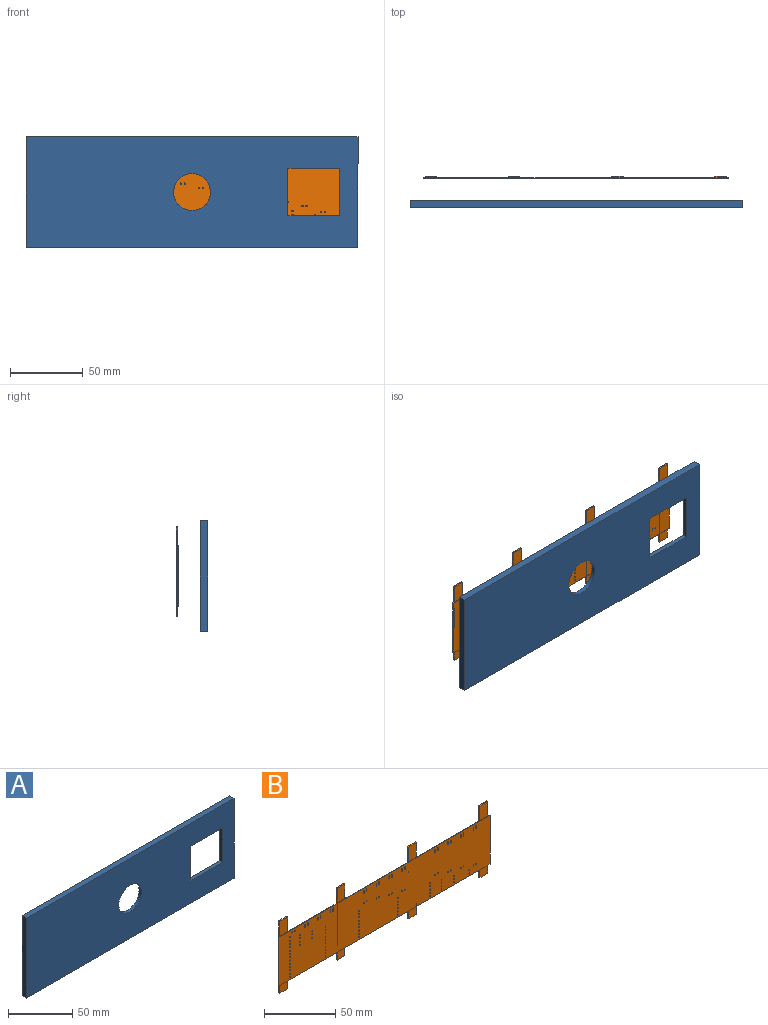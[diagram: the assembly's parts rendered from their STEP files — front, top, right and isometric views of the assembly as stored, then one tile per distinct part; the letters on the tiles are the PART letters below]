
ASSEMBLY  parts=2 mates=1
PART A: 48 faces, bbox 228.6x5.1x76.2 mm
  f0: plane 228.6x76.2mm, normal (0,-1,0), area 15738.4mm2, adj f11,f12,f13,f14,f43,f44,f45,f46
  f1: plane 210.9x62.26mm, normal (0,1,0), area 7928.5mm2, adj f3,f4,f5,f6,f7,f8,f9,f10
  f2: plane 228.6x76.2mm, normal (0,1,0), area 7810mm2, adj f3,f4,f5,f6,f7,f8,f9,f10
  f3: plane 48.84x2.03mm, normal (0,0,1), area 99.3mm2, adj f1,f2,f37,f42
  f4: plane 62.81x2.03mm, normal (0,0,1), area 127.6mm2, adj f1,f2,f33,f39
  f5: plane 2.03x1.61mm, normal (0,0,1), area 3.3mm2, adj f1,f2,f18,f36
  f6: plane 62.81x2.03mm, normal (0,0,1), area 127.6mm2, adj f1,f2,f31,f34
  f7: plane 48.84x2.03mm, normal (0,0,-1), area 99.3mm2, adj f1,f2,f25,f29
  f8: plane 62.81x2.03mm, normal (0,0,-1), area 127.6mm2, adj f1,f2,f19,f26
  f9: plane 2.03x1.61mm, normal (0,0,-1), area 3.3mm2, adj f1,f2,f18,f23
  f10: plane 62.81x2.03mm, normal (0,0,-1), area 127.6mm2, adj f1,f2,f20,f22
  f11: plane 228.6x5.08mm, normal (0,0,-1), area 1161.3mm2, adj f0,f2,f12,f14
  f12: plane 76.2x5.08mm, normal (1,0,0), area 387.1mm2, adj f0,f2,f11,f13
  f13: plane 228.6x5.08mm, normal (0,0,1), area 1161.3mm2, adj f0,f2,f12,f14
  f14: plane 76.2x5.08mm, normal (-1,0,0), area 387.1mm2, adj f0,f2,f11,f13
  f15: plane 2.03x1.59mm, normal (0,0,1), area 3.2mm2, adj f1,f2,f16,f40
  f16: plane 42.44x2.03mm, normal (1,0,0), area 86.2mm2, adj f1,f2,f15,f17
  f17: plane 2.03x1.59mm, normal (0,0,-1), area 3.2mm2, adj f1,f2,f16,f28
  f18: plane 42.44x2.03mm, normal (-1,0,0), area 86.2mm2, adj f1,f2,f5,f9
  f19: plane 12.51x2.03mm, normal (1,0,0), area 25.4mm2, adj f1,f2,f8,f21
  f20: plane 12.51x2.03mm, normal (-1,0,0), area 25.4mm2, adj f1,f2,f10,f21
  f21: plane 8.31x2.03mm, normal (0,0,-1), area 16.9mm2, adj f1,f2,f19,f20
  f22: plane 12.51x2.03mm, normal (1,0,0), area 25.4mm2, adj f1,f2,f10,f24
  f23: plane 12.51x2.03mm, normal (-1,0,0), area 25.4mm2, adj f1,f2,f9,f24
  f24: plane 8.31x2.03mm, normal (0,0,-1), area 16.9mm2, adj f1,f2,f22,f23
  f25: plane 12.51x2.03mm, normal (1,0,0), area 25.4mm2, adj f1,f2,f7,f27
  f26: plane 12.51x2.03mm, normal (-1,0,0), area 25.4mm2, adj f1,f2,f8,f27
  f27: plane 8.31x2.03mm, normal (0,0,-1), area 16.9mm2, adj f1,f2,f25,f26
  f28: plane 12.51x2.03mm, normal (1,0,0), area 25.4mm2, adj f1,f2,f17,f30
  f29: plane 12.51x2.03mm, normal (-1,0,0), area 25.4mm2, adj f1,f2,f7,f30
  f30: plane 8.31x2.03mm, normal (0,0,-1), area 16.9mm2, adj f1,f2,f28,f29
  f31: plane 7.3x2.03mm, normal (-1,0,0), area 14.8mm2, adj f1,f2,f6,f32
  f32: plane 8.31x2.03mm, normal (0,0,1), area 16.9mm2, adj f1,f2,f31,f33
  f33: plane 7.3x2.03mm, normal (1,0,0), area 14.8mm2, adj f1,f2,f4,f32
  f34: plane 7.3x2.03mm, normal (1,0,0), area 14.8mm2, adj f1,f2,f6,f35
  f35: plane 8.31x2.03mm, normal (0,0,1), area 16.9mm2, adj f1,f2,f34,f36
  f36: plane 7.3x2.03mm, normal (-1,0,0), area 14.8mm2, adj f1,f2,f5,f35
  f37: plane 7.3x2.03mm, normal (1,0,0), area 14.8mm2, adj f1,f2,f3,f38
  f38: plane 8.31x2.03mm, normal (0,0,1), area 16.9mm2, adj f1,f2,f37,f39
  f39: plane 7.3x2.03mm, normal (-1,0,0), area 14.8mm2, adj f1,f2,f4,f38
  f40: plane 7.3x2.03mm, normal (1,0,0), area 14.8mm2, adj f1,f2,f15,f41
  f41: plane 8.31x2.03mm, normal (0,0,1), area 16.9mm2, adj f1,f2,f40,f42
  f42: plane 7.3x2.03mm, normal (-1,0,0), area 14.8mm2, adj f1,f2,f3,f41
  f43: cylinder r=12.7mm len=25.4mm, axis (0,-1,0), area 243.2mm2, adj f0,f1
  f44: plane 35.56x3.05mm, normal (0,0,1), area 108.4mm2, adj f0,f1,f45,f47
  f45: plane 33.02x3.05mm, normal (1,0,0), area 100.6mm2, adj f0,f1,f44,f46
  f46: plane 35.56x3.05mm, normal (0,0,-1), area 108.4mm2, adj f0,f1,f45,f47
  f47: plane 33.02x3.05mm, normal (-1,0,0), area 100.6mm2, adj f0,f1,f44,f46
PART B: 159 faces, bbox 210.5x1.5x61.9 mm
  f0: plane 42.06x1.6mm, normal (0,1,0), area 67.3mm2, adj f4,f6,f7,f33
  f1: plane 49.23x42.06mm, normal (0,1,0), area 2044.8mm2, adj f4,f6,f26,f35,f38,f53,f54,f63
  f2: plane 63.2x42.06mm, normal (0,1,0), area 2635.9mm2, adj f4,f6,f12,f19,f39,f40,f41,f42
  f3: plane 63.2x42.06mm, normal (0,1,0), area 2635.3mm2, adj f4,f6,f14,f28,f45,f46,f47,f48
  f4: plane 210.52x0.51mm, normal (0,0,-1), area 106.9mm2, adj f0,f1,f2,f3,f5,f7,f8,f9
  f5: plane 42.06x0.51mm, normal (1,0,0), area 21.4mm2, adj f4,f6,f8,f9
  f6: plane 210.52x0.51mm, normal (0,0,1), area 106.9mm2, adj f0,f1,f2,f3,f5,f7,f8,f9
  f7: plane 42.06x0.51mm, normal (-1,0,0), area 21.4mm2, adj f0,f4,f6,f8
  f8: plane 210.52x42.06mm, normal (0,-1,0), area 8783.9mm2, adj f4,f5,f6,f7,f38,f39,f40,f41
  f9: plane 42.06x1.6mm, normal (0,1,0), area 67.3mm2, adj f4,f5,f6,f21
  f10: plane 7.93x7.11mm, normal (0,-1,0), area 56.4mm2, adj f4,f12,f13,f14
  f11: plane 7.93x1.02mm, normal (0,0,1), area 8.1mm2, adj f12,f14,f15,f16
  f12: plane 61.87x1.02mm, normal (1,0,0), area 62.9mm2, adj f2,f10,f11,f13,f15,f16
  f13: plane 7.93x1.02mm, normal (0,0,-1), area 8.1mm2, adj f10,f12,f14,f15
  f14: plane 61.87x1.02mm, normal (-1,0,0), area 62.9mm2, adj f3,f10,f11,f13,f15,f16
  f15: plane 61.87x7.93mm, normal (0,1,0), area 490.3mm2, adj f11,f12,f13,f14
  f16: plane 12.7x7.93mm, normal (0,-1,0), area 100.6mm2, adj f6,f11,f12,f14
  f17: plane 7.93x7.11mm, normal (0,-1,0), area 56.4mm2, adj f4,f18,f19,f21
  f18: plane 7.93x1.02mm, normal (0,0,-1), area 8.1mm2, adj f17,f19,f21,f22
  f19: plane 61.87x1.02mm, normal (-1,0,0), area 62.9mm2, adj f2,f17,f18,f20,f22,f23
  f20: plane 7.93x1.02mm, normal (0,0,1), area 8.1mm2, adj f19,f21,f22,f23
  f21: plane 61.87x1.02mm, normal (1,0,0), area 62.9mm2, adj f9,f17,f18,f20,f22,f23
  f22: plane 61.87x7.93mm, normal (0,1,0), area 490.3mm2, adj f18,f19,f20,f21
  f23: plane 12.7x7.93mm, normal (0,-1,0), area 100.6mm2, adj f6,f19,f20,f21
  f24: plane 7.93x7.11mm, normal (0,-1,0), area 56.4mm2, adj f4,f25,f26,f28
  f25: plane 7.93x1.02mm, normal (0,0,-1), area 8.1mm2, adj f24,f26,f28,f29
  f26: plane 61.87x1.02mm, normal (-1,0,0), area 62.9mm2, adj f1,f24,f25,f27,f29,f30
  f27: plane 7.93x1.02mm, normal (0,0,1), area 8.1mm2, adj f26,f28,f29,f30
  f28: plane 61.87x1.02mm, normal (1,0,0), area 62.9mm2, adj f3,f24,f25,f27,f29,f30
  f29: plane 61.87x7.93mm, normal (0,1,0), area 490.3mm2, adj f25,f26,f27,f28
  f30: plane 12.7x7.93mm, normal (0,-1,0), area 100.6mm2, adj f6,f26,f27,f28
  f31: plane 7.93x7.11mm, normal (0,-1,0), area 56.4mm2, adj f4,f32,f33,f35
  f32: plane 7.93x1.02mm, normal (0,0,-1), area 8.1mm2, adj f31,f33,f35,f36
  f33: plane 61.87x1.02mm, normal (-1,0,0), area 62.9mm2, adj f0,f31,f32,f34,f36,f37
  f34: plane 7.93x1.02mm, normal (0,0,1), area 8.1mm2, adj f33,f35,f36,f37
  f35: plane 61.87x1.02mm, normal (1,0,0), area 62.9mm2, adj f1,f31,f32,f34,f36,f37
  f36: plane 61.87x7.93mm, normal (0,1,0), area 490.3mm2, adj f32,f33,f34,f35
  f37: plane 12.7x7.93mm, normal (0,-1,0), area 100.6mm2, adj f6,f33,f34,f35
  f38: cylinder r=0.43mm len=0.86mm, axis (0,-1,0), area 1.4mm2, adj f1,f8
  f39: cylinder r=0.43mm len=0.86mm, axis (0,-1,0), area 1.4mm2, adj f2,f8
  f40: cylinder r=0.43mm len=0.86mm, axis (0,-1,0), area 1.4mm2, adj f2,f8
  f41: cylinder r=0.43mm len=0.86mm, axis (0,-1,0), area 1.4mm2, adj f2,f8
  f42: cylinder r=0.43mm len=0.86mm, axis (0,-1,0), area 1.4mm2, adj f2,f8
  f43: cylinder r=0.43mm len=0.86mm, axis (0,-1,0), area 1.4mm2, adj f2,f8
  f44: cylinder r=0.43mm len=0.86mm, axis (0,-1,0), area 1.4mm2, adj f2,f8
  f45: cylinder r=0.43mm len=0.86mm, axis (0,-1,0), area 1.4mm2, adj f3,f8
  f46: cylinder r=0.43mm len=0.86mm, axis (0,-1,0), area 1.4mm2, adj f3,f8
  f47: cylinder r=0.43mm len=0.86mm, axis (0,-1,0), area 1.4mm2, adj f3,f8
  f48: cylinder r=0.43mm len=0.86mm, axis (0,-1,0), area 1.4mm2, adj f3,f8
  f49: cylinder r=0.43mm len=0.86mm, axis (0,-1,0), area 1.4mm2, adj f3,f8
  f50: cylinder r=0.43mm len=0.86mm, axis (0,-1,0), area 1.4mm2, adj f3,f8
  f51: cylinder r=0.43mm len=0.86mm, axis (0,-1,0), area 1.4mm2, adj f3,f8
  f52: cylinder r=0.43mm len=0.86mm, axis (0,-1,0), area 1.4mm2, adj f3,f8
  f53: cylinder r=0.43mm len=0.86mm, axis (0,-1,0), area 1.4mm2, adj f1,f8
  f54: cylinder r=0.43mm len=0.86mm, axis (0,-1,0), area 1.4mm2, adj f1,f8
  f55: cylinder r=0.43mm len=0.86mm, axis (0,-1,0), area 1.4mm2, adj f3,f8
  f56: cylinder r=0.43mm len=0.86mm, axis (0,-1,0), area 1.4mm2, adj f2,f8
  f57: cylinder r=0.43mm len=0.86mm, axis (0,-1,0), area 1.4mm2, adj f2,f8
  f58: cylinder r=0.43mm len=0.86mm, axis (0,-1,0), area 1.4mm2, adj f2,f8
  f59: cylinder r=0.43mm len=0.86mm, axis (0,-1,0), area 1.4mm2, adj f3,f8
  f60: cylinder r=0.43mm len=0.86mm, axis (0,-1,0), area 1.4mm2, adj f3,f8
  f61: cylinder r=0.43mm len=0.86mm, axis (0,-1,0), area 1.4mm2, adj f3,f8
  f62: cylinder r=0.43mm len=0.86mm, axis (0,-1,0), area 1.4mm2, adj f3,f8
  f63: cylinder r=0.43mm len=0.86mm, axis (0,-1,0), area 1.4mm2, adj f1,f8
  f64: cylinder r=0.43mm len=0.86mm, axis (0,-1,0), area 1.4mm2, adj f1,f8
  f65: cylinder r=0.43mm len=0.86mm, axis (0,-1,0), area 1.4mm2, adj f1,f8
  f66: cylinder r=0.43mm len=0.86mm, axis (0,-1,0), area 1.4mm2, adj f1,f8
  f67: cylinder r=0.43mm len=0.86mm, axis (0,-1,0), area 1.4mm2, adj f2,f8
  f68: cylinder r=0.43mm len=0.86mm, axis (0,-1,0), area 1.4mm2, adj f2,f8
  f69: cylinder r=0.43mm len=0.86mm, axis (0,-1,0), area 1.4mm2, adj f2,f8
  f70: cylinder r=0.43mm len=0.86mm, axis (0,-1,0), area 1.4mm2, adj f1,f8
  f71: cylinder r=0.43mm len=0.86mm, axis (0,-1,0), area 1.4mm2, adj f2,f8
  f72: cylinder r=0.43mm len=0.86mm, axis (0,-1,0), area 1.4mm2, adj f2,f8
  f73: cylinder r=0.43mm len=0.86mm, axis (0,-1,0), area 1.4mm2, adj f2,f8
  f74: cylinder r=0.43mm len=0.86mm, axis (0,-1,0), area 1.4mm2, adj f2,f8
  f75: cylinder r=0.43mm len=0.86mm, axis (0,-1,0), area 1.4mm2, adj f2,f8
  f76: cylinder r=0.43mm len=0.86mm, axis (0,-1,0), area 1.4mm2, adj f2,f8
  f77: cylinder r=0.43mm len=0.86mm, axis (0,-1,0), area 1.4mm2, adj f2,f8
  f78: cylinder r=0.43mm len=0.86mm, axis (0,-1,0), area 1.4mm2, adj f2,f8
  f79: cylinder r=0.43mm len=0.86mm, axis (0,-1,0), area 1.4mm2, adj f2,f8
  f80: cylinder r=0.43mm len=0.86mm, axis (0,-1,0), area 1.4mm2, adj f2,f8
  f81: cylinder r=0.43mm len=0.86mm, axis (0,-1,0), area 1.4mm2, adj f1,f8
  f82: cylinder r=0.43mm len=0.86mm, axis (0,-1,0), area 1.4mm2, adj f1,f8
  f83: cylinder r=0.43mm len=0.86mm, axis (0,-1,0), area 1.4mm2, adj f1,f8
  f84: cylinder r=0.43mm len=0.86mm, axis (0,-1,0), area 1.4mm2, adj f1,f8
  f85: cylinder r=0.43mm len=0.86mm, axis (0,-1,0), area 1.4mm2, adj f1,f8
  f86: cylinder r=0.43mm len=0.86mm, axis (0,-1,0), area 1.4mm2, adj f1,f8
  f87: cylinder r=0.43mm len=0.86mm, axis (0,-1,0), area 1.4mm2, adj f3,f8
  f88: cylinder r=0.43mm len=0.86mm, axis (0,-1,0), area 1.4mm2, adj f3,f8
  f89: cylinder r=0.43mm len=0.86mm, axis (0,-1,0), area 1.4mm2, adj f3,f8
  f90: cylinder r=0.43mm len=0.86mm, axis (0,-1,0), area 1.4mm2, adj f3,f8
  f91: cylinder r=0.43mm len=0.86mm, axis (0,-1,0), area 1.4mm2, adj f3,f8
  f92: cylinder r=0.43mm len=0.86mm, axis (0,-1,0), area 1.4mm2, adj f3,f8
  f93: cylinder r=0.43mm len=0.86mm, axis (0,-1,0), area 1.4mm2, adj f3,f8
  f94: cylinder r=0.43mm len=0.86mm, axis (0,-1,0), area 1.4mm2, adj f3,f8
  f95: cylinder r=0.43mm len=0.86mm, axis (0,-1,0), area 1.4mm2, adj f1,f8
  f96: cylinder r=0.43mm len=0.86mm, axis (0,-1,0), area 1.4mm2, adj f1,f8
  f97: cylinder r=0.43mm len=0.86mm, axis (0,-1,0), area 1.4mm2, adj f1,f8
  f98: cylinder r=0.43mm len=0.86mm, axis (0,-1,0), area 1.4mm2, adj f1,f8
  f99: cylinder r=0.43mm len=0.86mm, axis (0,-1,0), area 1.4mm2, adj f1,f8
  f100: cylinder r=0.43mm len=0.86mm, axis (0,-1,0), area 1.4mm2, adj f1,f8
  f101: cylinder r=0.43mm len=0.86mm, axis (0,-1,0), area 1.4mm2, adj f1,f8
  f102: cylinder r=0.43mm len=0.86mm, axis (0,-1,0), area 1.4mm2, adj f1,f8
  f103: cylinder r=0.43mm len=0.86mm, axis (0,-1,0), area 1.4mm2, adj f1,f8
  f104: cylinder r=0.43mm len=0.86mm, axis (0,-1,0), area 1.4mm2, adj f1,f8
  f105: cylinder r=0.43mm len=0.86mm, axis (0,-1,0), area 1.4mm2, adj f1,f8
  f106: cylinder r=0.43mm len=0.86mm, axis (0,-1,0), area 1.4mm2, adj f1,f8
  f107: cylinder r=0.43mm len=0.86mm, axis (0,-1,0), area 1.4mm2, adj f3,f8
  f108: cylinder r=0.43mm len=0.86mm, axis (0,-1,0), area 1.4mm2, adj f3,f8
  f109: cylinder r=0.43mm len=0.86mm, axis (0,-1,0), area 1.4mm2, adj f3,f8
  f110: cylinder r=0.43mm len=0.86mm, axis (0,-1,0), area 1.4mm2, adj f3,f8
  f111: cylinder r=0.43mm len=0.86mm, axis (0,-1,0), area 1.4mm2, adj f2,f8
  f112: cylinder r=0.43mm len=0.86mm, axis (0,-1,0), area 1.4mm2, adj f1,f8
  f113: cylinder r=0.43mm len=0.86mm, axis (0,-1,0), area 1.4mm2, adj f1,f8
  f114: cylinder r=0.43mm len=0.86mm, axis (0,-1,0), area 1.4mm2, adj f1,f8
  f115: cylinder r=0.43mm len=0.86mm, axis (0,-1,0), area 1.4mm2, adj f1,f8
  f116: cylinder r=0.43mm len=0.86mm, axis (0,-1,0), area 1.4mm2, adj f2,f8
  f117: cylinder r=0.43mm len=0.86mm, axis (0,-1,0), area 1.4mm2, adj f2,f8
  f118: cylinder r=0.43mm len=0.86mm, axis (0,-1,0), area 1.4mm2, adj f2,f8
  f119: cylinder r=0.43mm len=0.86mm, axis (0,-1,0), area 1.4mm2, adj f1,f8
  f120: cylinder r=0.43mm len=0.86mm, axis (0,-1,0), area 1.4mm2, adj f1,f8
  f121: cylinder r=0.43mm len=0.86mm, axis (0,-1,0), area 1.4mm2, adj f1,f8
  f122: cylinder r=0.43mm len=0.86mm, axis (0,-1,0), area 1.4mm2, adj f1,f8
  f123: cylinder r=0.43mm len=0.86mm, axis (0,-1,0), area 1.4mm2, adj f1,f8
  f124: cylinder r=0.43mm len=0.86mm, axis (0,-1,0), area 1.4mm2, adj f1,f8
  f125: cylinder r=0.43mm len=0.86mm, axis (0,-1,0), area 1.4mm2, adj f1,f8
  f126: cylinder r=0.43mm len=0.86mm, axis (0,-1,0), area 1.4mm2, adj f1,f8
  f127: cylinder r=0.43mm len=0.86mm, axis (0,-1,0), area 1.4mm2, adj f1,f8
  f128: cylinder r=0.43mm len=0.86mm, axis (0,-1,0), area 1.4mm2, adj f2,f8
  f129: cylinder r=0.43mm len=0.86mm, axis (0,-1,0), area 1.4mm2, adj f2,f8
  f130: cylinder r=0.43mm len=0.86mm, axis (0,-1,0), area 1.4mm2, adj f2,f8
  f131: cylinder r=0.43mm len=0.86mm, axis (0,-1,0), area 1.4mm2, adj f2,f8
  f132: cylinder r=0.43mm len=0.86mm, axis (0,-1,0), area 1.4mm2, adj f2,f8
  f133: cylinder r=0.43mm len=0.86mm, axis (0,-1,0), area 1.4mm2, adj f2,f8
  f134: cylinder r=0.43mm len=0.86mm, axis (0,-1,0), area 1.4mm2, adj f2,f8
  f135: cylinder r=0.43mm len=0.86mm, axis (0,-1,0), area 1.4mm2, adj f1,f8
  f136: cylinder r=0.43mm len=0.86mm, axis (0,-1,0), area 1.4mm2, adj f3,f8
  f137: cylinder r=0.43mm len=0.86mm, axis (0,-1,0), area 1.4mm2, adj f3,f8
  f138: cylinder r=0.43mm len=0.86mm, axis (0,-1,0), area 1.4mm2, adj f3,f8
  f139: cylinder r=0.43mm len=0.86mm, axis (0,-1,0), area 1.4mm2, adj f1,f8
  f140: cylinder r=0.43mm len=0.86mm, axis (0,-1,0), area 1.4mm2, adj f1,f8
  f141: cylinder r=0.43mm len=0.86mm, axis (0,-1,0), area 1.4mm2, adj f1,f8
  f142: cylinder r=0.43mm len=0.86mm, axis (0,-1,0), area 1.4mm2, adj f1,f8
  f143: cylinder r=0.43mm len=0.86mm, axis (0,-1,0), area 1.4mm2, adj f3,f8
  f144: cylinder r=0.43mm len=0.86mm, axis (0,-1,0), area 1.4mm2, adj f3,f8
  f145: cylinder r=0.43mm len=0.86mm, axis (0,-1,0), area 1.4mm2, adj f3,f8
  f146: cylinder r=0.43mm len=0.86mm, axis (0,-1,0), area 1.4mm2, adj f3,f8
  f147: cylinder r=0.43mm len=0.86mm, axis (0,-1,0), area 1.4mm2, adj f3,f8
  f148: cylinder r=0.43mm len=0.86mm, axis (0,-1,0), area 1.4mm2, adj f3,f8
  f149: cylinder r=0.43mm len=0.86mm, axis (0,-1,0), area 1.4mm2, adj f3,f8
  f150: cylinder r=0.43mm len=0.86mm, axis (0,-1,0), area 1.4mm2, adj f3,f8
  f151: cylinder r=0.43mm len=0.86mm, axis (0,-1,0), area 1.4mm2, adj f2,f8
  f152: cylinder r=0.43mm len=0.86mm, axis (0,-1,0), area 1.4mm2, adj f2,f8
  f153: cylinder r=0.43mm len=0.86mm, axis (0,-1,0), area 1.4mm2, adj f2,f8
  f154: cylinder r=0.43mm len=0.86mm, axis (0,-1,0), area 1.4mm2, adj f2,f8
  f155: cylinder r=0.43mm len=0.86mm, axis (0,-1,0), area 1.4mm2, adj f3,f8
  f156: cylinder r=0.43mm len=0.86mm, axis (0,-1,0), area 1.4mm2, adj f3,f8
  f157: cylinder r=0.43mm len=0.86mm, axis (0,-1,0), area 1.4mm2, adj f3,f8
  f158: cylinder r=0.43mm len=0.86mm, axis (0,-1,0), area 1.4mm2, adj f2,f8
PLACE A t=(24,21.99,-3.26)mm fixed
PLACE B t=(23.94,37.35,-3.23)mm
MATE slider A.f43 <-> B.f8  axis (0,1,0) through (24,19.96,-3.26)mm
